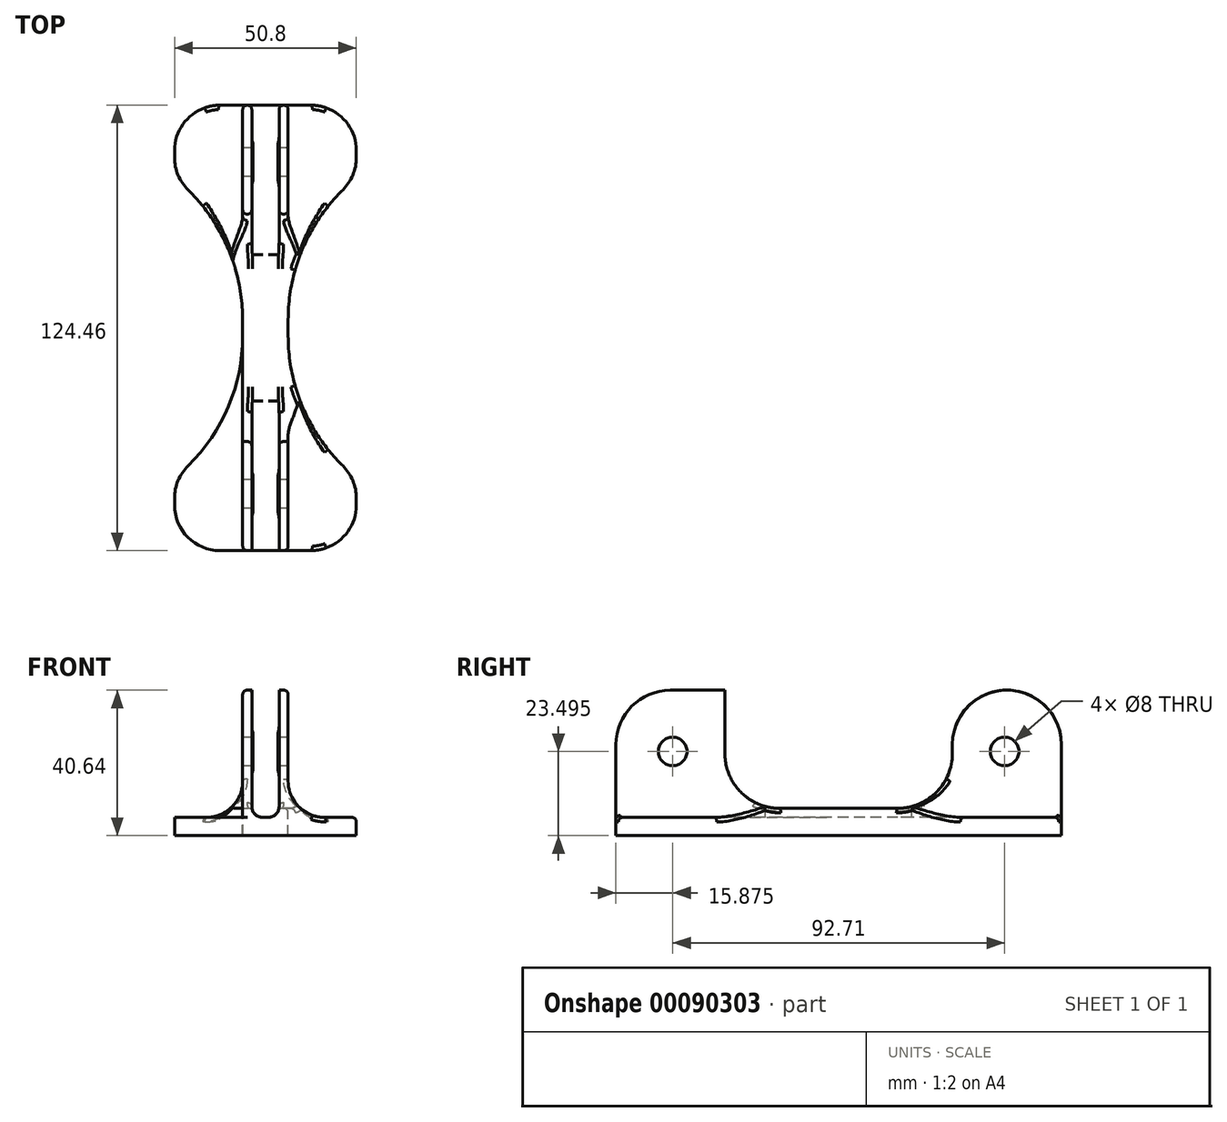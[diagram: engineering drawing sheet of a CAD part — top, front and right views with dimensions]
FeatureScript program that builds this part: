
annotation { "Feature Type Name" : "Feature", "Feature Type Description" : "" }
export const myFeature = defineFeature(function(context is Context, id is Id, definition is map)
    precondition{}
    {
        {
            var Q0;
            Q0=qCreatedBy(makeId("Top.planeOp"),FACE);
            var sketch = newSketch(context, id + "F0", { "sketchPlane" : qUnion([Q0])});
            skLineSegment(sketch, "E0.bottom", {"start": v(6.35, 62.23) * mm, "end": v(-6.35, 62.23) * mm});
            skLineSegment(sketch, "E0.top", {"start": v(6.35, -62.23) * mm, "end": v(-6.35, -62.23) * mm});
            skLineSegment(sketch, "E0.left", {"start": v(6.35, 62.23) * mm, "end": v(6.35, -62.23) * mm});
            skLineSegment(sketch, "E0.right", {"start": v(-6.35, 62.23) * mm, "end": v(-6.35, -62.23) * mm});
            skPoint(sketch, "E0.middle", {"position": v(0, 0) * mm});
            skLineSegment(sketch, "E1.bottom", {"start": v(-25.4, 62.23) * mm, "end": v(25.4, 62.23) * mm});
            skLineSegment(sketch, "E1.top", {"start": v(-25.4, 41.9) * mm, "end": v(25.4, 41.91) * mm});
            skLineSegment(sketch, "E1.left", {"start": v(-25.4, 62.23) * mm, "end": v(-25.4, 41.9) * mm});
            skLineSegment(sketch, "E1.right", {"start": v(25.4, 62.23) * mm, "end": v(25.4, 41.91) * mm});
            skLineSegment(sketch, "E2.bottom", {"start": v(-25.4, -62.23) * mm, "end": v(25.4, -62.23) * mm});
            skLineSegment(sketch, "E2.top", {"start": v(-25.4, -41.91) * mm, "end": v(25.4, -41.91) * mm});
            skLineSegment(sketch, "E2.left", {"start": v(-25.4, -62.23) * mm, "end": v(-25.4, -41.91) * mm});
            skLineSegment(sketch, "E2.right", {"start": v(25.4, -62.23) * mm, "end": v(25.4, -41.91) * mm});
            skSolve(sketch);
        }
        {
            var Q0;
            Q0 = qSketchRegion(id + "F0", true);
            extrude(context, id + "F1", {"entities" : qUnion([Q0]), "depth" : 5.08 * mm});
        }
        {
            var Q0;
            Q0=makeQuery(id+"F1.opExtrude","CAP_FACE",FACE,{"disambiguationData":[OSD([sQuery(id+"F0.wireOp",EDGE,"E0.left"),sQuery(id+"F0.wireOp",EDGE,"E0.right"),sQuery(id+"F0.wireOp",EDGE,"E1.bottom"),sQuery(id+"F0.wireOp",EDGE,"E1.top"),sQuery(id+"F0.wireOp",EDGE,"E1.left"),sQuery(id+"F0.wireOp",EDGE,"E1.right"),sQuery(id+"F0.wireOp",EDGE,"E2.bottom"),sQuery(id+"F0.wireOp",EDGE,"E2.top"),sQuery(id+"F0.wireOp",EDGE,"E2.left"),sQuery(id+"F0.wireOp",EDGE,"E2.right")])],"isStart":false});
            var sketch = newSketch(context, id + "F2", { "sketchPlane" : qUnion([Q0])});
            skLineSegment(sketch, "E3.bottom", {"start": v(-6.35, 62.23) * mm, "end": v(-3.81, 62.23) * mm});
            skLineSegment(sketch, "E3.top", {"start": v(-6.35, -62.23) * mm, "end": v(-3.8, -62.23) * mm});
            skLineSegment(sketch, "E3.left", {"start": v(-6.35, 62.23) * mm, "end": v(-6.35, -62.23) * mm});
            skLineSegment(sketch, "E3.right", {"start": v(-3.81, 62.23) * mm, "end": v(-3.8, -62.23) * mm});
            skLineSegment(sketch, "E4.bottom", {"start": v(6.35, 62.23) * mm, "end": v(3.8, 62.23) * mm});
            skLineSegment(sketch, "E4.top", {"start": v(6.35, -62.23) * mm, "end": v(3.81, -62.23) * mm});
            skLineSegment(sketch, "E4.left", {"start": v(6.35, 62.23) * mm, "end": v(6.35, -62.23) * mm});
            skLineSegment(sketch, "E4.right", {"start": v(3.8, 62.23) * mm, "end": v(3.81, -62.23) * mm});
            skSolve(sketch);
        }
        {
            var Q0;
            Q0 = qSketchRegion(id + "F2", true);
            extrude(context, id + "F3", {"entities" : qUnion([Q0]), "operationType" : NewBodyOperationType.ADD, "depth" : 35.56 * mm});
        }
        {
            var Q0;
            Q0=makeQuery(id+"F3.boolean.opBoolean","MERGE",FACE,{"derivedFrom":[makeQuery(id+"F1.opExtrude","SWEPT_FACE",FACE,{"disambiguationData":[OSD([sQuery(id+"F0.wireOp",EDGE,"E0.right")])]}),makeQuery(id+"F3.opExtrude","SWEPT_FACE",FACE,{"disambiguationData":[OSD([sQuery(id+"F2.wireOp",EDGE,"E3.left")])]})]});
            var sketch = newSketch(context, id + "F4", { "sketchPlane" : qUnion([Q0])});
            skCircle(sketch, "E5", {"center": v(-46.35, 23.5) * mm, "radius": 4 * mm});
            skCircle(sketch, "E6", {"center": v(46.36, 23.5) * mm, "radius": 4 * mm});
            skCircle(sketch, "E7", {"center": v(-46.35, 23.5) * mm, "radius": 5.27 * mm});
            skCircle(sketch, "E8", {"center": v(46.36, 23.5) * mm, "radius": 5.27 * mm});
            skSolve(sketch);
        }
        {
            var Q0;
            Q0=makeQuery(id+"F4.imprint","IMPRINT",FACE,{"disambiguationData":[TD([[makeQuery(id+"F4.imprint","IMPRINT",EDGE,{"derivedFrom":sQuery(id+"F4.wireOp",EDGE,"E5")}),-1.0]])]});
            var Q1;
            Q1=makeQuery(id+"F4.imprint","IMPRINT",FACE,{"disambiguationData":[TD([[makeQuery(id+"F4.imprint","IMPRINT",EDGE,{"derivedFrom":sQuery(id+"F4.wireOp",EDGE,"E6")}),-1.0]])]});
            var Q2;
            Q2=makeQuery(id+"F3.boolean.opBoolean","MERGE",FACE,{"derivedFrom":[makeQuery(id+"F1.opExtrude","SWEPT_FACE",FACE,{"disambiguationData":[OSD([sQuery(id+"F0.wireOp",EDGE,"E0.left")])]}),makeQuery(id+"F3.opExtrude","SWEPT_FACE",FACE,{"disambiguationData":[OSD([sQuery(id+"F2.wireOp",EDGE,"E4.left")])]})]});
            extrude(context, id + "F5", {"entities" : qUnion([Q0, Q1]), "operationType" : NewBodyOperationType.ADD, "endBound" : BoundingType.UP_TO_SURFACE, "oppositeDirection" : true, "endBoundEntityFace" : qUnion([Q2]), "depth" : 25.4 * mm});
        }
        {
            var Q0;
            Q0=makeQuery(id+"F4.imprint","IMPRINT",FACE,{"disambiguationData":[TD([[makeQuery(id+"F4.imprint","IMPRINT",EDGE,{"derivedFrom":sQuery(id+"F4.wireOp",EDGE,"E5")}),1.0]])]});
            var Q1;
            Q1=makeQuery(id+"F4.imprint","IMPRINT",FACE,{"disambiguationData":[TD([[makeQuery(id+"F4.imprint","IMPRINT",EDGE,{"derivedFrom":sQuery(id+"F4.wireOp",EDGE,"E6")}),1.0]])]});
            var Q2;
            Q2=makeQuery(id+"F3.boolean.opBoolean","MERGE",FACE,{"derivedFrom":[makeQuery(id+"F1.opExtrude","SWEPT_FACE",FACE,{"disambiguationData":[OSD([sQuery(id+"F0.wireOp",EDGE,"E0.left")])]}),makeQuery(id+"F3.opExtrude","SWEPT_FACE",FACE,{"disambiguationData":[OSD([sQuery(id+"F2.wireOp",EDGE,"E4.left")])]})]});
            extrude(context, id + "F6", {"entities" : qUnion([Q0, Q1, Q2]), "operationType" : NewBodyOperationType.REMOVE, "endBound" : BoundingType.THROUGH_ALL, "oppositeDirection" : true, "depth" : 25.4 * mm});
        }
        {
            var Q0;
            Q0=qCreatedBy(makeId("Front.planeOp"),FACE);
            var sketch = newSketch(context, id + "F7", { "sketchPlane" : qUnion([Q0])});
            skLineSegment(sketch, "E9.bottom", {"start": v(-3.5, 35.3) * mm, "end": v(3.5, 35.3) * mm});
            skLineSegment(sketch, "E9.top", {"start": v(-3.5, 13.06) * mm, "end": v(3.5, 13.06) * mm});
            skLineSegment(sketch, "E9.left", {"start": v(-3.5, 35.3) * mm, "end": v(-3.5, 13.06) * mm});
            skLineSegment(sketch, "E9.right", {"start": v(3.5, 35.3) * mm, "end": v(3.5, 13.06) * mm});
            skPoint(sketch, "E9.middle", {"position": v(0, 24.18) * mm});
            skSolve(sketch);
        }
        {
            var Q0;
            Q0=makeQuery(id+"F7.imprint","IMPRINT",FACE,{"disambiguationData":[TD([[makeQuery(id+"F7.imprint","IMPRINT",EDGE,{"derivedFrom":sQuery(id+"F7.wireOp",EDGE,"E9.bottom")}),-1.0]])]});
            extrude(context, id + "F8", {"entities" : qUnion([Q0]), "operationType" : NewBodyOperationType.REMOVE, "endBound" : BoundingType.SYMMETRIC, "oppositeDirection" : true, "depth" : 127 * mm});
        }
        {
            var Q0;
            Q0=makeQuery(id+"F3.boolean.opBoolean","MERGE",FACE,{"derivedFrom":[makeQuery(id+"F1.opExtrude","SWEPT_FACE",FACE,{"disambiguationData":[OSD([sQuery(id+"F0.wireOp",EDGE,"E0.left")])]}),makeQuery(id+"F3.opExtrude","SWEPT_FACE",FACE,{"disambiguationData":[OSD([sQuery(id+"F2.wireOp",EDGE,"E4.left")])]})]});
            var sketch = newSketch(context, id + "F9", { "sketchPlane" : qUnion([Q0])});
            skLineSegment(sketch, "E10.bottom", {"start": v(-31.75, 40.64) * mm, "end": v(31.75, 40.64) * mm});
            skLineSegment(sketch, "E10.top", {"start": v(-31.75, 7.62) * mm, "end": v(31.75, 7.62) * mm});
            skLineSegment(sketch, "E10.left", {"start": v(-31.75, 40.64) * mm, "end": v(-31.75, 7.62) * mm});
            skLineSegment(sketch, "E10.right", {"start": v(31.75, 40.64) * mm, "end": v(31.75, 7.62) * mm});
            skSolve(sketch);
        }
        {
            var Q0;
            Q0 = qSketchRegion(id + "F9", true);
            extrude(context, id + "F10", {"entities" : qUnion([Q0]), "operationType" : NewBodyOperationType.REMOVE, "endBound" : BoundingType.THROUGH_ALL, "oppositeDirection" : true, "depth" : 25.4 * mm});
        }
        {
            var Q0;
            Q0=makeQuery(id+"F3.opExtrude","CAP_EDGE",EDGE,{"disambiguationData":[OSD([sQuery(id+"F2.wireOp",EDGE,"E4.top")])],"isStart":false});
            var Q1;
            Q1=makeQuery(id+"F3.opExtrude","CAP_EDGE",EDGE,{"disambiguationData":[OSD([sQuery(id+"F2.wireOp",EDGE,"E3.top")])],"isStart":false});
            var Q2;
            Q2=makeQuery(id+"F10.boolean.opBoolean","COPY",EDGE,{"disambiguationData":[OD(0.0)],"derivedFrom":makeQuery(id+"F10.opExtrude","SWEPT_EDGE",EDGE,{"disambiguationData":[OSD([sQuery(id+"F2.wireOp",EDGE,"E4.left"),sQuery(id+"F9.wireOp",EDGE,"E10.bottom"),sQuery(id+"F9.wireOp",EDGE,"E10.left")])]})});
            var Q3;
            Q3=makeQuery(id+"F10.boolean.opBoolean","COPY",EDGE,{"disambiguationData":[OD(1.0)],"derivedFrom":makeQuery(id+"F10.opExtrude","SWEPT_EDGE",EDGE,{"disambiguationData":[OSD([sQuery(id+"F2.wireOp",EDGE,"E4.left"),sQuery(id+"F9.wireOp",EDGE,"E10.bottom"),sQuery(id+"F9.wireOp",EDGE,"E10.left")])]})});
            var Q4;
            Q4=makeQuery(id+"F10.boolean.opBoolean","COPY",EDGE,{"disambiguationData":[OD(0.0)],"derivedFrom":makeQuery(id+"F10.opExtrude","SWEPT_EDGE",EDGE,{"disambiguationData":[OSD([sQuery(id+"F2.wireOp",EDGE,"E4.left"),sQuery(id+"F9.wireOp",EDGE,"E10.bottom"),sQuery(id+"F9.wireOp",EDGE,"E10.right")])]})});
            var Q5;
            Q5=makeQuery(id+"F3.opExtrude","CAP_EDGE",EDGE,{"disambiguationData":[OSD([sQuery(id+"F2.wireOp",EDGE,"E4.bottom")])],"isStart":false});
            var Q6;
            Q6=makeQuery(id+"F10.boolean.opBoolean","COPY",EDGE,{"disambiguationData":[OD(1.0)],"derivedFrom":makeQuery(id+"F10.opExtrude","SWEPT_EDGE",EDGE,{"disambiguationData":[OSD([sQuery(id+"F2.wireOp",EDGE,"E4.left"),sQuery(id+"F9.wireOp",EDGE,"E10.bottom"),sQuery(id+"F9.wireOp",EDGE,"E10.right")])]})});
            var Q7;
            Q7=makeQuery(id+"F3.opExtrude","CAP_EDGE",EDGE,{"disambiguationData":[OSD([sQuery(id+"F2.wireOp",EDGE,"E3.bottom")])],"isStart":false});
            var Q8;
            Q8=makeQuery(id+"F10.boolean.opBoolean","COPY",EDGE,{"disambiguationData":[OD(0.0)],"derivedFrom":makeQuery(id+"F10.opExtrude","SWEPT_EDGE",EDGE,{"disambiguationData":[OSD([sQuery(id+"F9.wireOp",EDGE,"E10.top"),sQuery(id+"F9.wireOp",EDGE,"E10.left")])]})});
            var Q9;
            Q9=makeQuery(id+"F10.boolean.opBoolean","COPY",EDGE,{"disambiguationData":[OD(1.0)],"derivedFrom":makeQuery(id+"F10.opExtrude","SWEPT_EDGE",EDGE,{"disambiguationData":[OSD([sQuery(id+"F9.wireOp",EDGE,"E10.top"),sQuery(id+"F9.wireOp",EDGE,"E10.left")])]})});
            var Q10;
            Q10=makeQuery(id+"F10.boolean.opBoolean","COPY",EDGE,{"disambiguationData":[OD(1.0)],"derivedFrom":makeQuery(id+"F10.opExtrude","SWEPT_EDGE",EDGE,{"disambiguationData":[OSD([sQuery(id+"F9.wireOp",EDGE,"E10.top"),sQuery(id+"F9.wireOp",EDGE,"E10.right")])]})});
            var Q11;
            Q11=makeQuery(id+"F10.boolean.opBoolean","COPY",EDGE,{"disambiguationData":[OD(0.0)],"derivedFrom":makeQuery(id+"F10.opExtrude","SWEPT_EDGE",EDGE,{"disambiguationData":[OSD([sQuery(id+"F9.wireOp",EDGE,"E10.top"),sQuery(id+"F9.wireOp",EDGE,"E10.right")])]})});
            fillet(context, id + "F11", {"entities" : qUnion([Q0, Q1, Q2, Q3, Q4, Q5, Q6, Q7, Q8, Q9, Q10, Q11]), "radius" : 15.24 * mm, "tangentPropagation" : true, "allowEdgeOverflow" : false});
        }
        {
            var Q0;
            {var subQ3=sQuery(id+"F0.wireOp",EDGE,"E2.bottom");var subQ4=sQuery(id+"F2.wireOp",EDGE,"E4.left");Q0=makeQuery(id+"F3.boolean.opBoolean","SPLIT",EDGE,{"disambiguationData":[TD([makeQuery(id+"F1.opExtrude","SWEPT_FACE",FACE,{"disambiguationData":[OSD([subQ3])]})])],"derivedFrom":makeQuery(id+"F3.opExtrude","CAP_EDGE",EDGE,{"disambiguationData":[OSD([subQ4])],"isStart":true})});}
            var Q1;
            {var subQ3=sQuery(id+"F0.wireOp",EDGE,"E1.bottom");var subQ4=sQuery(id+"F2.wireOp",EDGE,"E4.left");Q1=makeQuery(id+"F3.boolean.opBoolean","SPLIT",EDGE,{"disambiguationData":[TD([makeQuery(id+"F1.opExtrude","SWEPT_FACE",FACE,{"disambiguationData":[OSD([subQ3])]})])],"derivedFrom":makeQuery(id+"F3.opExtrude","CAP_EDGE",EDGE,{"disambiguationData":[OSD([subQ4])],"isStart":true})});}
            var Q2;
            {var subQ3=sQuery(id+"F0.wireOp",EDGE,"E2.bottom");var subQ4=sQuery(id+"F2.wireOp",EDGE,"E3.left");Q2=makeQuery(id+"F3.boolean.opBoolean","SPLIT",EDGE,{"disambiguationData":[TD([makeQuery(id+"F1.opExtrude","SWEPT_FACE",FACE,{"disambiguationData":[OSD([subQ3])]})])],"derivedFrom":makeQuery(id+"F3.opExtrude","CAP_EDGE",EDGE,{"disambiguationData":[OSD([subQ4])],"isStart":true})});}
            var Q3;
            {var subQ3=sQuery(id+"F0.wireOp",EDGE,"E1.bottom");var subQ4=sQuery(id+"F2.wireOp",EDGE,"E3.left");Q3=makeQuery(id+"F3.boolean.opBoolean","SPLIT",EDGE,{"disambiguationData":[TD([makeQuery(id+"F1.opExtrude","SWEPT_FACE",FACE,{"disambiguationData":[OSD([subQ3])]})])],"derivedFrom":makeQuery(id+"F3.opExtrude","CAP_EDGE",EDGE,{"disambiguationData":[OSD([subQ4])],"isStart":true})});}
            fillet(context, id + "F12", {"entities" : qUnion([Q0, Q1, Q2, Q3]), "radius" : 10.16 * mm, "tangentPropagation" : true, "allowEdgeOverflow" : false});
        }
        {
            var Q0;
            Q0=makeQuery(id+"F1.opExtrude","SWEPT_EDGE",EDGE,{"disambiguationData":[OSD([sQuery(id+"F0.wireOp",EDGE,"E0.left"),sQuery(id+"F0.wireOp",EDGE,"E2.top")])]});
            var Q1;
            Q1=makeQuery(id+"F1.opExtrude","SWEPT_EDGE",EDGE,{"disambiguationData":[OSD([sQuery(id+"F0.wireOp",EDGE,"E0.left"),sQuery(id+"F0.wireOp",EDGE,"E1.top")])]});
            var Q2;
            Q2=makeQuery(id+"F1.opExtrude","SWEPT_EDGE",EDGE,{"disambiguationData":[OSD([sQuery(id+"F0.wireOp",EDGE,"E0.right"),sQuery(id+"F0.wireOp",EDGE,"E1.top")])]});
            var Q3;
            Q3=makeQuery(id+"F1.opExtrude","SWEPT_EDGE",EDGE,{"disambiguationData":[OSD([sQuery(id+"F0.wireOp",EDGE,"E0.right"),sQuery(id+"F0.wireOp",EDGE,"E2.top")])]});
            fillet(context, id + "F13", {"entities" : qUnion([Q0, Q1, Q2, Q3]), "radius" : 50.8 * mm, "tangentPropagation" : true, "allowEdgeOverflow" : false});
        }
        {
            var Q0;
            Q0=makeQuery(id+"F1.opExtrude","SWEPT_EDGE",EDGE,{"disambiguationData":[OSD([sQuery(id+"F0.wireOp",EDGE,"E1.bottom"),sQuery(id+"F0.wireOp",EDGE,"E1.left")])]});
            var Q1;
            Q1=makeQuery(id+"F13.opFillet","BLEND_EDGE",EDGE,{"blendedFrom":[makeQuery(id+"F1.opExtrude","SWEPT_EDGE",EDGE,{"disambiguationData":[OSD([sQuery(id+"F0.wireOp",EDGE,"E0.right"),sQuery(id+"F0.wireOp",EDGE,"E1.top")])]}),makeQuery(id+"F1.opExtrude","SWEPT_FACE",FACE,{"disambiguationData":[OSD([sQuery(id+"F0.wireOp",EDGE,"E1.left")])]})],"blendedInto":[makeQuery(id+"F1.opExtrude","SWEPT_FACE",FACE,{"disambiguationData":[OSD([sQuery(id+"F0.wireOp",EDGE,"E1.left")])]})]});
            var Q2;
            Q2=makeQuery(id+"F13.opFillet","BLEND_EDGE",EDGE,{"blendedFrom":[makeQuery(id+"F1.opExtrude","SWEPT_EDGE",EDGE,{"disambiguationData":[OSD([sQuery(id+"F0.wireOp",EDGE,"E0.right"),sQuery(id+"F0.wireOp",EDGE,"E2.top")])]}),makeQuery(id+"F1.opExtrude","SWEPT_FACE",FACE,{"disambiguationData":[OSD([sQuery(id+"F0.wireOp",EDGE,"E2.left")])]})],"blendedInto":[makeQuery(id+"F1.opExtrude","SWEPT_FACE",FACE,{"disambiguationData":[OSD([sQuery(id+"F0.wireOp",EDGE,"E2.left")])]})]});
            var Q3;
            Q3=makeQuery(id+"F1.opExtrude","SWEPT_EDGE",EDGE,{"disambiguationData":[OSD([sQuery(id+"F0.wireOp",EDGE,"E2.bottom"),sQuery(id+"F0.wireOp",EDGE,"E2.left")])]});
            var Q4;
            Q4=makeQuery(id+"F1.opExtrude","SWEPT_EDGE",EDGE,{"disambiguationData":[OSD([sQuery(id+"F0.wireOp",EDGE,"E1.bottom"),sQuery(id+"F0.wireOp",EDGE,"E1.right")])]});
            var Q5;
            Q5=makeQuery(id+"F13.opFillet","BLEND_EDGE",EDGE,{"blendedFrom":[makeQuery(id+"F1.opExtrude","SWEPT_EDGE",EDGE,{"disambiguationData":[OSD([sQuery(id+"F0.wireOp",EDGE,"E0.left"),sQuery(id+"F0.wireOp",EDGE,"E2.top")])]}),makeQuery(id+"F1.opExtrude","SWEPT_FACE",FACE,{"disambiguationData":[OSD([sQuery(id+"F0.wireOp",EDGE,"E2.right")])]})],"blendedInto":[makeQuery(id+"F1.opExtrude","SWEPT_FACE",FACE,{"disambiguationData":[OSD([sQuery(id+"F0.wireOp",EDGE,"E2.right")])]})]});
            var Q6;
            Q6=makeQuery(id+"F13.opFillet","BLEND_EDGE",EDGE,{"blendedFrom":[makeQuery(id+"F1.opExtrude","SWEPT_EDGE",EDGE,{"disambiguationData":[OSD([sQuery(id+"F0.wireOp",EDGE,"E0.left"),sQuery(id+"F0.wireOp",EDGE,"E1.top")])]}),makeQuery(id+"F1.opExtrude","SWEPT_FACE",FACE,{"disambiguationData":[OSD([sQuery(id+"F0.wireOp",EDGE,"E1.right")])]})],"blendedInto":[makeQuery(id+"F1.opExtrude","SWEPT_FACE",FACE,{"disambiguationData":[OSD([sQuery(id+"F0.wireOp",EDGE,"E1.right")])]})]});
            var Q7;
            Q7=makeQuery(id+"F1.opExtrude","SWEPT_EDGE",EDGE,{"disambiguationData":[OSD([sQuery(id+"F0.wireOp",EDGE,"E2.bottom"),sQuery(id+"F0.wireOp",EDGE,"E2.right")])]});
            fillet(context, id + "F14", {"entities" : qUnion([Q0, Q1, Q2, Q3, Q4, Q5, Q6, Q7]), "radius" : 12.7 * mm, "tangentPropagation" : true, "allowEdgeOverflow" : false});
        }
        {
            var Q0;
            Q0=makeQuery(id+"F3.opExtrude","CAP_EDGE",EDGE,{"disambiguationData":[OSD([sQuery(id+"F2.wireOp",EDGE,"E3.right")])],"isStart":true});
            var Q1;
            Q1=makeQuery(id+"F3.opExtrude","CAP_EDGE",EDGE,{"disambiguationData":[OSD([sQuery(id+"F2.wireOp",EDGE,"E4.right")])],"isStart":true});
            fillet(context, id + "F15", {"entities" : qUnion([Q0, Q1]), "radius" : 3.05 * mm, "tangentPropagation" : true, "allowEdgeOverflow" : false});
        }
        {
            var Q0;
            Q0=makeQuery(id+"F3.opExtrude","SWEPT_EDGE",EDGE,{"disambiguationData":[OSD([sQuery(id+"F0.wireOp",EDGE,"E2.bottom"),sQuery(id+"F2.wireOp",EDGE,"E4.top"),sQuery(id+"F2.wireOp",EDGE,"E4.left")])]});
            var Q1;
            Q1=makeQuery(id+"F11.opFillet","BLEND_EDGE",EDGE,{"blendedFrom":[makeQuery(id+"F3.opExtrude","CAP_EDGE",EDGE,{"disambiguationData":[OSD([sQuery(id+"F2.wireOp",EDGE,"E4.bottom")])],"isStart":false}),makeQuery(id+"F3.boolean.opBoolean","MERGE",FACE,{"derivedFrom":[makeQuery(id+"F1.opExtrude","SWEPT_FACE",FACE,{"disambiguationData":[OSD([sQuery(id+"F0.wireOp",EDGE,"E0.left")])]}),makeQuery(id+"F3.opExtrude","SWEPT_FACE",FACE,{"disambiguationData":[OSD([sQuery(id+"F2.wireOp",EDGE,"E4.left")])]})]})],"blendedInto":[makeQuery(id+"F3.boolean.opBoolean","MERGE",FACE,{"derivedFrom":[makeQuery(id+"F1.opExtrude","SWEPT_FACE",FACE,{"disambiguationData":[OSD([sQuery(id+"F0.wireOp",EDGE,"E0.left")])]}),makeQuery(id+"F3.opExtrude","SWEPT_FACE",FACE,{"disambiguationData":[OSD([sQuery(id+"F2.wireOp",EDGE,"E4.left")])]})]})]});
            var Q2;
            {var subQ0=sQuery(id+"F0.wireOp",EDGE,"E0.left");var subQ1=sQuery(id+"F9.wireOp",EDGE,"E10.top");var subQ2=sQuery(id+"F9.wireOp",EDGE,"E10.right");Q2=makeQuery(id+"F13.opFillet","BLEND_EDGE",EDGE,{"blendedFrom":[makeQuery(id+"F1.opExtrude","SWEPT_EDGE",EDGE,{"disambiguationData":[OSD([subQ0,sQuery(id+"F0.wireOp",EDGE,"E1.top")])]}),makeQuery(id+"F11.opFillet","BLEND_FACE",FACE,{"disambiguationData":[OSD([subQ1,subQ2]),TDD([makeQuery(id+"F10.boolean.opBoolean","COPY",EDGE,{"disambiguationData":[TD([makeQuery(id+"F1.opExtrude","SWEPT_FACE",FACE,{"disambiguationData":[OSD([subQ0])]})])],"derivedFrom":makeQuery(id+"F10.opExtrude","SWEPT_EDGE",EDGE,{"disambiguationData":[OSD([subQ1,subQ2])]})})])]})],"blendedInto":[makeQuery(id+"F11.opFillet","BLEND_FACE",FACE,{"disambiguationData":[OSD([subQ1,subQ2]),TDD([makeQuery(id+"F10.boolean.opBoolean","COPY",EDGE,{"disambiguationData":[TD([makeQuery(id+"F1.opExtrude","SWEPT_FACE",FACE,{"disambiguationData":[OSD([subQ0])]})])],"derivedFrom":makeQuery(id+"F10.opExtrude","SWEPT_EDGE",EDGE,{"disambiguationData":[OSD([subQ1,subQ2])]})})])]})]});}
            var Q3;
            Q3=makeQuery(id+"F15.opFillet","BLEND_EDGE",EDGE,{"blendedFrom":[makeQuery(id+"F3.opExtrude","CAP_EDGE",EDGE,{"disambiguationData":[OSD([sQuery(id+"F2.wireOp",EDGE,"E4.right")])],"isStart":true}),makeQuery(id+"F10.boolean.opBoolean","COPY",FACE,{"disambiguationData":[OD(0.0)],"derivedFrom":makeQuery(id+"F10.opExtrude","SWEPT_FACE",FACE,{"disambiguationData":[OSD([sQuery(id+"F9.wireOp",EDGE,"E10.top")])]})})],"blendedInto":[makeQuery(id+"F10.boolean.opBoolean","COPY",FACE,{"disambiguationData":[OD(0.0)],"derivedFrom":makeQuery(id+"F10.opExtrude","SWEPT_FACE",FACE,{"disambiguationData":[OSD([sQuery(id+"F9.wireOp",EDGE,"E10.top")])]})})]});
            var Q4;
            Q4=makeQuery(id+"F3.opExtrude","SWEPT_EDGE",EDGE,{"disambiguationData":[OSD([sQuery(id+"F0.wireOp",EDGE,"E2.bottom"),sQuery(id+"F2.wireOp",EDGE,"E3.top"),sQuery(id+"F2.wireOp",EDGE,"E3.left")])]});
            var Q5;
            Q5=makeQuery(id+"F13.opFillet","BLEND_EDGE",EDGE,{"blendedFrom":[makeQuery(id+"F1.opExtrude","SWEPT_EDGE",EDGE,{"disambiguationData":[OSD([sQuery(id+"F0.wireOp",EDGE,"E0.right"),sQuery(id+"F0.wireOp",EDGE,"E2.top")])]}),makeQuery(id+"F10.boolean.opBoolean","COPY",FACE,{"disambiguationData":[OD(1.0)],"derivedFrom":makeQuery(id+"F10.opExtrude","SWEPT_FACE",FACE,{"disambiguationData":[OSD([sQuery(id+"F9.wireOp",EDGE,"E10.top")])]})})],"blendedInto":[makeQuery(id+"F10.boolean.opBoolean","COPY",FACE,{"disambiguationData":[OD(1.0)],"derivedFrom":makeQuery(id+"F10.opExtrude","SWEPT_FACE",FACE,{"disambiguationData":[OSD([sQuery(id+"F9.wireOp",EDGE,"E10.top")])]})})]});
            var Q6;
            {var subQ0=sQuery(id+"F0.wireOp",EDGE,"E1.left");var subQ1=sQuery(id+"F0.wireOp",EDGE,"E1.top");var subQ2=sQuery(id+"F0.wireOp",EDGE,"E0.right");var subQ3=sQuery(id+"F0.wireOp",EDGE,"E1.bottom");Q6=makeQuery(id+"F13.opFillet","BLEND_EDGE",EDGE,{"blendedFrom":[makeQuery(id+"F1.opExtrude","SWEPT_EDGE",EDGE,{"disambiguationData":[OSD([subQ2,subQ1])]}),makeQuery(id+"F3.boolean.opBoolean","SPLIT",FACE,{"disambiguationData":[TD([makeQuery(id+"F1.opExtrude","SWEPT_FACE",FACE,{"disambiguationData":[OSD([subQ0])]})])],"derivedFrom":makeQuery(id+"F1.opExtrude","CAP_FACE",FACE,{"disambiguationData":[OSD([sQuery(id+"F0.wireOp",EDGE,"E0.left"),subQ2,subQ3,subQ1,subQ0,sQuery(id+"F0.wireOp",EDGE,"E1.right"),sQuery(id+"F0.wireOp",EDGE,"E2.bottom"),sQuery(id+"F0.wireOp",EDGE,"E2.top"),sQuery(id+"F0.wireOp",EDGE,"E2.left"),sQuery(id+"F0.wireOp",EDGE,"E2.right")])],"isStart":false})})],"blendedInto":[makeQuery(id+"F3.boolean.opBoolean","SPLIT",FACE,{"disambiguationData":[TD([makeQuery(id+"F1.opExtrude","SWEPT_FACE",FACE,{"disambiguationData":[OSD([subQ0])]})])],"derivedFrom":makeQuery(id+"F1.opExtrude","CAP_FACE",FACE,{"disambiguationData":[OSD([sQuery(id+"F0.wireOp",EDGE,"E0.left"),subQ2,subQ3,subQ1,subQ0,sQuery(id+"F0.wireOp",EDGE,"E1.right"),sQuery(id+"F0.wireOp",EDGE,"E2.bottom"),sQuery(id+"F0.wireOp",EDGE,"E2.top"),sQuery(id+"F0.wireOp",EDGE,"E2.left"),sQuery(id+"F0.wireOp",EDGE,"E2.right")])],"isStart":false})})]});}
            fillet(context, id + "F16", {"entities" : qUnion([Q0, Q1, Q2, Q3, Q4, Q5, Q6]), "radius" : 1.27 * mm, "tangentPropagation" : true, "allowEdgeOverflow" : false});
        }
        {
            var Q0;
            Q0=makeQuery(id+"F6.boolean.opBoolean","COPY",EDGE,{"derivedFrom":makeQuery(id+"F6.opExtrude","CAP_EDGE",EDGE,{"disambiguationData":[OSD([sQuery(id+"F4.wireOp",EDGE,"E5")])],"isStart":true})});
            var Q1;
            {var subQ0=sQuery(id+"F4.wireOp",EDGE,"E5");Q1=makeQuery(id+"F8.boolean.opBoolean","INTERSECT",EDGE,{"derivedFrom":[makeQuery(id+"F6.boolean.opBoolean","MERGE",FACE,{"derivedFrom":[makeQuery(id+"F5.opExtrude","SWEPT_FACE",FACE,{"disambiguationData":[OSD([subQ0])]}),makeQuery(id+"F6.opExtrude","SWEPT_FACE",FACE,{"disambiguationData":[OSD([subQ0])]})]}),makeQuery(id+"F8.opExtrude","SWEPT_FACE",FACE,{"disambiguationData":[OSD([sQuery(id+"F7.wireOp",EDGE,"E9.right")])]})]});}
            var Q2;
            {var subQ0=sQuery(id+"F2.wireOp",EDGE,"E4.left");var subQ1=sQuery(id+"F0.wireOp",EDGE,"E0.left");Q2=makeQuery(id+"F6.boolean.opBoolean","INTERSECT",EDGE,{"derivedFrom":[makeQuery(id+"F3.boolean.opBoolean","MERGE",FACE,{"derivedFrom":[makeQuery(id+"F1.opExtrude","SWEPT_FACE",FACE,{"disambiguationData":[OSD([subQ1])]}),makeQuery(id+"F3.opExtrude","SWEPT_FACE",FACE,{"disambiguationData":[OSD([subQ0])]})]}),makeQuery(id+"F6.opExtrude","SWEPT_FACE",FACE,{"disambiguationData":[OSD([sQuery(id+"F4.wireOp",EDGE,"E5")])]}),makeQuery(id+"F6.opExtrude","CAP_FACE",FACE,{"disambiguationData":[OSD([subQ1,subQ0])],"isStart":true})]});}
            var Q3;
            {var subQ0=sQuery(id+"F4.wireOp",EDGE,"E5");Q3=makeQuery(id+"F8.boolean.opBoolean","INTERSECT",EDGE,{"derivedFrom":[makeQuery(id+"F6.boolean.opBoolean","MERGE",FACE,{"derivedFrom":[makeQuery(id+"F5.opExtrude","SWEPT_FACE",FACE,{"disambiguationData":[OSD([subQ0])]}),makeQuery(id+"F6.opExtrude","SWEPT_FACE",FACE,{"disambiguationData":[OSD([subQ0])]})]}),makeQuery(id+"F8.opExtrude","SWEPT_FACE",FACE,{"disambiguationData":[OSD([sQuery(id+"F7.wireOp",EDGE,"E9.left")])]})]});}
            var Q4;
            Q4=makeQuery(id+"F6.boolean.opBoolean","COPY",EDGE,{"derivedFrom":makeQuery(id+"F6.opExtrude","CAP_EDGE",EDGE,{"disambiguationData":[OSD([sQuery(id+"F4.wireOp",EDGE,"E6")])],"isStart":true})});
            var Q5;
            {var subQ0=sQuery(id+"F4.wireOp",EDGE,"E6");Q5=makeQuery(id+"F8.boolean.opBoolean","INTERSECT",EDGE,{"derivedFrom":[makeQuery(id+"F6.boolean.opBoolean","MERGE",FACE,{"derivedFrom":[makeQuery(id+"F5.opExtrude","SWEPT_FACE",FACE,{"disambiguationData":[OSD([subQ0])]}),makeQuery(id+"F6.opExtrude","SWEPT_FACE",FACE,{"disambiguationData":[OSD([subQ0])]})]}),makeQuery(id+"F8.opExtrude","SWEPT_FACE",FACE,{"disambiguationData":[OSD([sQuery(id+"F7.wireOp",EDGE,"E9.left")])]})]});}
            var Q6;
            {var subQ0=sQuery(id+"F2.wireOp",EDGE,"E4.left");var subQ1=sQuery(id+"F0.wireOp",EDGE,"E0.left");Q6=makeQuery(id+"F6.boolean.opBoolean","INTERSECT",EDGE,{"derivedFrom":[makeQuery(id+"F3.boolean.opBoolean","MERGE",FACE,{"derivedFrom":[makeQuery(id+"F1.opExtrude","SWEPT_FACE",FACE,{"disambiguationData":[OSD([subQ1])]}),makeQuery(id+"F3.opExtrude","SWEPT_FACE",FACE,{"disambiguationData":[OSD([subQ0])]})]}),makeQuery(id+"F6.opExtrude","SWEPT_FACE",FACE,{"disambiguationData":[OSD([sQuery(id+"F4.wireOp",EDGE,"E6")])]}),makeQuery(id+"F6.opExtrude","CAP_FACE",FACE,{"disambiguationData":[OSD([subQ1,subQ0])],"isStart":true})]});}
            var Q7;
            {var subQ0=sQuery(id+"F4.wireOp",EDGE,"E6");Q7=makeQuery(id+"F8.boolean.opBoolean","INTERSECT",EDGE,{"derivedFrom":[makeQuery(id+"F6.boolean.opBoolean","MERGE",FACE,{"derivedFrom":[makeQuery(id+"F5.opExtrude","SWEPT_FACE",FACE,{"disambiguationData":[OSD([subQ0])]}),makeQuery(id+"F6.opExtrude","SWEPT_FACE",FACE,{"disambiguationData":[OSD([subQ0])]})]}),makeQuery(id+"F8.opExtrude","SWEPT_FACE",FACE,{"disambiguationData":[OSD([sQuery(id+"F7.wireOp",EDGE,"E9.right")])]})]});}
            fillet(context, id + "F17", {"entities" : qUnion([Q0, Q1, Q2, Q3, Q4, Q5, Q6, Q7]), "radius" : 0.25 * mm, "tangentPropagation" : true, "allowEdgeOverflow" : false});
        }
        {
            var Q0;
            Q0=makeQuery(id+"F5.boolean.opBoolean","INTERSECT",EDGE,{"derivedFrom":[makeQuery(id+"F3.opExtrude","SWEPT_FACE",FACE,{"disambiguationData":[OSD([sQuery(id+"F2.wireOp",EDGE,"E3.right")])]}),makeQuery(id+"F5.opExtrude","SWEPT_FACE",FACE,{"disambiguationData":[OSD([sQuery(id+"F4.wireOp",EDGE,"E8")])]})]});
            var Q1;
            Q1=makeQuery(id+"F5.boolean.opBoolean","INTERSECT",EDGE,{"derivedFrom":[makeQuery(id+"F3.opExtrude","SWEPT_FACE",FACE,{"disambiguationData":[OSD([sQuery(id+"F2.wireOp",EDGE,"E4.right")])]}),makeQuery(id+"F5.opExtrude","SWEPT_FACE",FACE,{"disambiguationData":[OSD([sQuery(id+"F4.wireOp",EDGE,"E8")])]})]});
            var Q2;
            Q2=makeQuery(id+"F5.boolean.opBoolean","INTERSECT",EDGE,{"derivedFrom":[makeQuery(id+"F3.opExtrude","SWEPT_FACE",FACE,{"disambiguationData":[OSD([sQuery(id+"F2.wireOp",EDGE,"E4.right")])]}),makeQuery(id+"F5.opExtrude","SWEPT_FACE",FACE,{"disambiguationData":[OSD([sQuery(id+"F4.wireOp",EDGE,"E7")])]})]});
            var Q3;
            Q3=makeQuery(id+"F5.boolean.opBoolean","INTERSECT",EDGE,{"derivedFrom":[makeQuery(id+"F3.opExtrude","SWEPT_FACE",FACE,{"disambiguationData":[OSD([sQuery(id+"F2.wireOp",EDGE,"E3.right")])]}),makeQuery(id+"F5.opExtrude","SWEPT_FACE",FACE,{"disambiguationData":[OSD([sQuery(id+"F4.wireOp",EDGE,"E7")])]})]});
            fillet(context, id + "F18", {"entities" : qUnion([Q0, Q1, Q2, Q3]), "radius" : 5.08 * mm, "tangentPropagation" : true, "allowEdgeOverflow" : false});
        }
        {
            var Q0;
            Q0=makeQuery(id+"F18.opFillet","BLEND_EDGE",EDGE,{"blendedFrom":[makeQuery(id+"F5.boolean.opBoolean","INTERSECT",EDGE,{"derivedFrom":[makeQuery(id+"F3.opExtrude","SWEPT_FACE",FACE,{"disambiguationData":[OSD([sQuery(id+"F2.wireOp",EDGE,"E3.right")])]}),makeQuery(id+"F5.opExtrude","SWEPT_FACE",FACE,{"disambiguationData":[OSD([sQuery(id+"F4.wireOp",EDGE,"E7")])]})]}),makeQuery(id+"F8.boolean.opBoolean","COPY",FACE,{"disambiguationData":[OD(0.0)],"derivedFrom":makeQuery(id+"F8.opExtrude","SWEPT_FACE",FACE,{"disambiguationData":[OSD([sQuery(id+"F7.wireOp",EDGE,"E9.left")])]})})],"blendedInto":[makeQuery(id+"F8.boolean.opBoolean","COPY",FACE,{"disambiguationData":[OD(0.0)],"derivedFrom":makeQuery(id+"F8.opExtrude","SWEPT_FACE",FACE,{"disambiguationData":[OSD([sQuery(id+"F7.wireOp",EDGE,"E9.left")])]})})]});
            var Q1;
            Q1=makeQuery(id+"F18.opFillet","BLEND_EDGE",EDGE,{"blendedFrom":[makeQuery(id+"F5.boolean.opBoolean","INTERSECT",EDGE,{"derivedFrom":[makeQuery(id+"F3.opExtrude","SWEPT_FACE",FACE,{"disambiguationData":[OSD([sQuery(id+"F2.wireOp",EDGE,"E4.right")])]}),makeQuery(id+"F5.opExtrude","SWEPT_FACE",FACE,{"disambiguationData":[OSD([sQuery(id+"F4.wireOp",EDGE,"E7")])]})]}),makeQuery(id+"F8.boolean.opBoolean","COPY",FACE,{"disambiguationData":[OD(0.0)],"derivedFrom":makeQuery(id+"F8.opExtrude","SWEPT_FACE",FACE,{"disambiguationData":[OSD([sQuery(id+"F7.wireOp",EDGE,"E9.right")])]})})],"blendedInto":[makeQuery(id+"F8.boolean.opBoolean","COPY",FACE,{"disambiguationData":[OD(0.0)],"derivedFrom":makeQuery(id+"F8.opExtrude","SWEPT_FACE",FACE,{"disambiguationData":[OSD([sQuery(id+"F7.wireOp",EDGE,"E9.right")])]})})]});
            var Q2;
            Q2=makeQuery(id+"F18.opFillet","BLEND_EDGE",EDGE,{"blendedFrom":[makeQuery(id+"F5.boolean.opBoolean","INTERSECT",EDGE,{"derivedFrom":[makeQuery(id+"F3.opExtrude","SWEPT_FACE",FACE,{"disambiguationData":[OSD([sQuery(id+"F2.wireOp",EDGE,"E4.right")])]}),makeQuery(id+"F5.opExtrude","SWEPT_FACE",FACE,{"disambiguationData":[OSD([sQuery(id+"F4.wireOp",EDGE,"E8")])]})]}),makeQuery(id+"F8.boolean.opBoolean","COPY",FACE,{"disambiguationData":[OD(1.0)],"derivedFrom":makeQuery(id+"F8.opExtrude","SWEPT_FACE",FACE,{"disambiguationData":[OSD([sQuery(id+"F7.wireOp",EDGE,"E9.right")])]})})],"blendedInto":[makeQuery(id+"F8.boolean.opBoolean","COPY",FACE,{"disambiguationData":[OD(1.0)],"derivedFrom":makeQuery(id+"F8.opExtrude","SWEPT_FACE",FACE,{"disambiguationData":[OSD([sQuery(id+"F7.wireOp",EDGE,"E9.right")])]})})]});
            var Q3;
            Q3=makeQuery(id+"F18.opFillet","BLEND_EDGE",EDGE,{"blendedFrom":[makeQuery(id+"F5.boolean.opBoolean","INTERSECT",EDGE,{"derivedFrom":[makeQuery(id+"F3.opExtrude","SWEPT_FACE",FACE,{"disambiguationData":[OSD([sQuery(id+"F2.wireOp",EDGE,"E3.right")])]}),makeQuery(id+"F5.opExtrude","SWEPT_FACE",FACE,{"disambiguationData":[OSD([sQuery(id+"F4.wireOp",EDGE,"E8")])]})]}),makeQuery(id+"F8.boolean.opBoolean","COPY",FACE,{"disambiguationData":[OD(1.0)],"derivedFrom":makeQuery(id+"F8.opExtrude","SWEPT_FACE",FACE,{"disambiguationData":[OSD([sQuery(id+"F7.wireOp",EDGE,"E9.left")])]})})],"blendedInto":[makeQuery(id+"F8.boolean.opBoolean","COPY",FACE,{"disambiguationData":[OD(1.0)],"derivedFrom":makeQuery(id+"F8.opExtrude","SWEPT_FACE",FACE,{"disambiguationData":[OSD([sQuery(id+"F7.wireOp",EDGE,"E9.left")])]})})]});
            fillet(context, id + "F19", {"entities" : qUnion([Q0, Q1, Q2, Q3]), "radius" : 0.25 * mm, "tangentPropagation" : true, "allowEdgeOverflow" : false});
        }
    });
